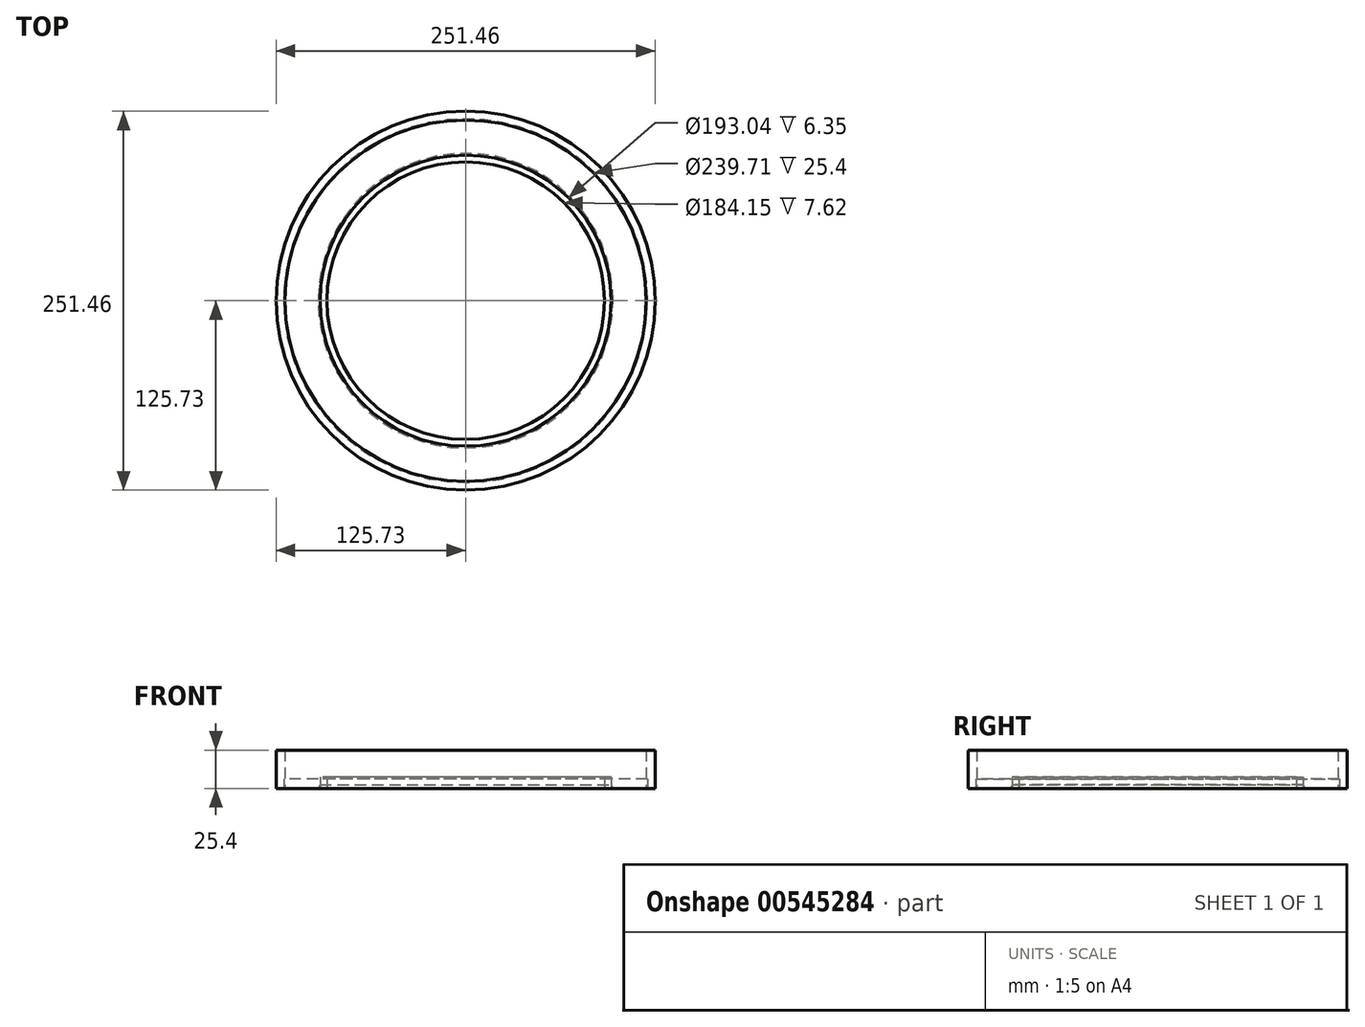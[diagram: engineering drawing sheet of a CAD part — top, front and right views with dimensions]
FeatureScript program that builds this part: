
annotation { "Feature Type Name" : "Feature", "Feature Type Description" : "" }
export const myFeature = defineFeature(function(context is Context, id is Id, definition is map)
    precondition{}
    {
        {
            var Q0;
            Q0=qCreatedBy(makeId("Top.planeOp"),FACE);
            var sketch = newSketch(context, id + "F0", { "sketchPlane" : qUnion([Q0])});
            skCircle(sketch, "E0", {"center": v(0, 0) * mm, "radius": 92.08 * mm});
            skCircle(sketch, "E1", {"center": v(0, 0) * mm, "radius": 96.52 * mm});
            skSolve(sketch);
        }
        {
            var Q0;
            Q0=makeQuery(id+"F0.imprint","IMPRINT",FACE,{"disambiguationData":[TD([[makeQuery(id+"F0.imprint","IMPRINT",EDGE,{"derivedFrom":sQuery(id+"F0.wireOp",EDGE,"E0")}),-1.0]])]});
            extrude(context, id + "F1", {"entities" : qUnion([Q0]), "depth" : 7.62 * mm, "offsetDistance" : 25.4 * mm});
        }
        {
            var Q0;
            Q0=qCreatedBy(makeId("Front.planeOp"),FACE);
            var sketch = newSketch(context, id + "F2", { "sketchPlane" : qUnion([Q0])});
            skLineSegment(sketch, "E2", {"start": v(0, 0) * mm, "end": v(96.52, 0) * mm, "construction": true});
            skLineSegment(sketch, "E3", {"start": v(96.52, 0) * mm, "end": v(96.52, 2.54) * mm});
            skLineSegment(sketch, "E4", {"start": v(0, 0) * mm, "end": v(0, 19.7) * mm});
            skLineSegment(sketch, "E5", {"start": v(96.52, 0) * mm, "end": v(97.8, 0) * mm});
            skLineSegment(sketch, "E6", {"start": v(97.8, 0) * mm, "end": v(96.52, 2.54) * mm});
            skSolve(sketch);
        }
        {
            var Q0;
            Q0=makeQuery(id+"F2.imprint","IMPRINT",FACE,{"disambiguationData":[TD([[makeQuery(id+"F2.imprint","IMPRINT",EDGE,{"derivedFrom":sQuery(id+"F2.wireOp",EDGE,"E3")}),-1.0]])]});
            var Q1;
            Q1=sQuery(id+"F2.wireOp",EDGE,"E4");
            revolve(context, id + "F3", {"operationType" : NewBodyOperationType.ADD, "entities" : qUnion([Q0]), "axis" : qUnion([Q1]), "revolveType" : RevolveType.FULL});
        }
        {
            var Q0;
            Q0=qCreatedBy(makeId("Top.planeOp"),FACE);
            var sketch = newSketch(context, id + "F4", { "sketchPlane" : qUnion([Q0])});
            skCircle(sketch, "E7", {"center": v(0, 0) * mm, "radius": 119.86 * mm});
            skCircle(sketch, "E8", {"center": v(0, 0) * mm, "radius": 125.73 * mm});
            skSolve(sketch);
        }
        {
            var Q0;
            Q0=makeQuery(id+"F4.imprint","IMPRINT",FACE,{"disambiguationData":[TD([[makeQuery(id+"F4.imprint","IMPRINT",EDGE,{"derivedFrom":sQuery(id+"F4.wireOp",EDGE,"E7")}),-1.0]])]});
            extrude(context, id + "F5", {"entities" : qUnion([Q0]), "depth" : 25.4 * mm, "offsetDistance" : 25.4 * mm});
        }
        {
            var Q0;
            Q0=qCreatedBy(makeId("Top.planeOp"),FACE);
            var sketch = newSketch(context, id + "F6", { "sketchPlane" : qUnion([Q0])});
            skCircle(sketch, "E9", {"center": v(0, 0) * mm, "radius": 120.65 * mm});
            skCircle(sketch, "E10", {"center": v(0, 0) * mm, "radius": 96.52 * mm});
            skSolve(sketch);
        }
        {
            var Q0;
            Q0=makeQuery(id+"F6.imprint","IMPRINT",FACE,{"disambiguationData":[TD([[makeQuery(id+"F6.imprint","IMPRINT",EDGE,{"derivedFrom":sQuery(id+"F6.wireOp",EDGE,"E9")}),1.0]])]});
            extrude(context, id + "F7", {"entities" : qUnion([Q0]), "depth" : 6.35 * mm, "offsetDistance" : 25.4 * mm});
        }
    });
